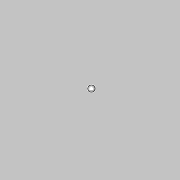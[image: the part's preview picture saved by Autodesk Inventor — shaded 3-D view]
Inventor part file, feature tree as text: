
AUTODESK INVENTOR PART (.ipt)
format: ipt  version: 2017 (Build 210142000, 142)  size: 137,216 bytes
history: native  units: mm
features: extrude x5, sketch x4, revolve x1, thread x1, fillet x1
ambient origin geometry x8: Origin, YZ Plane, XZ Plane, XY Plane, X Axis, Y Axis, Z Axis, Center Point
bodies: Solid1 (feature_tree)
feature tree (12):
  sketch  "Sketch1"  dims[d2=52.0mm d4=105.0mm]
  revolve  "Revolution1"  [1 undecoded]
  extrude  "Extrusion1"  Depth=38.0mm
  extrude  "Extrusion2"  Depth=11.0mm
  extrude  "Extrusion3"  TaperAngle=90.0deg  [1 undecoded]
  extrude  "Extrusion4"  Depth=8.726646mm
  thread  "Thread1"  [1 undecoded]
  extrude  "Extrusion5"  Depth=38.0mm
  fillet  "Fillet1"  Radius=10.0mm
  sketch  "Sketch2"  dims[d5=27.0mm d6=38.0mm]
  sketch  "Sketch3"  dims[d7=42.0mm d8=11.0mm]
  sketch  "Sketch4"  dims[d9=52.0mm d10=90.0deg d11=8.726646mm d12=6.0mm d13=38.0mm d14=10.0mm d15=0.0mm d16=24.0mm d17=24.0mm d18=24.0mm d19=0.0mm d20=12.0mm d21=10.0mm d22=0.0mm d23=20.9mm d24=20.0mm d25=0.0mm d26=10.0mm d27=0.0mm d28=25.0mm d29=10.0mm d30=3.0mm d31=6.0mm d32=1.0mm d33=0.0mm d34=1.0mm d35=-12.0mm]
note: 3 required parameter values undecoded (feature->parameter linkage not recoverable at this tier; creation-order binding heuristic only, values carry confidence <= 0.55)